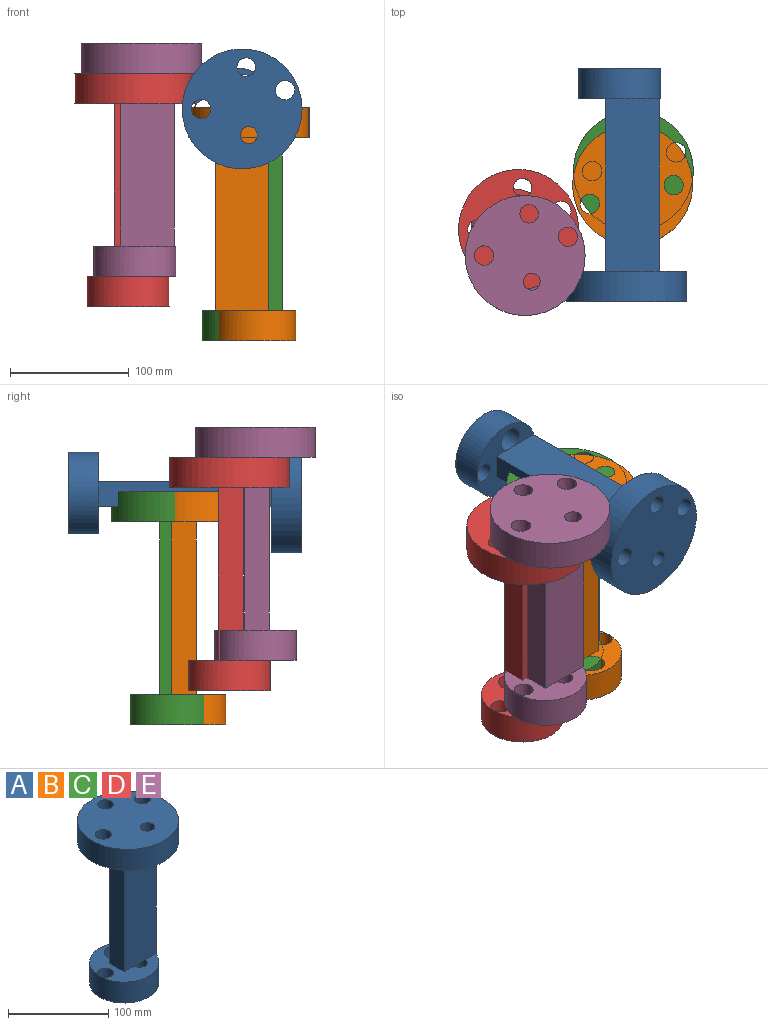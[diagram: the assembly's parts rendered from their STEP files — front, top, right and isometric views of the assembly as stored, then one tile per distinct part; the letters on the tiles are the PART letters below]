
ASSEMBLY  parts=5 mates=4
PART A: 21 faces, bbox 100.7x100.7x195.8 mm
  f0: plane 68.85x67.57mm, normal (0,0,1), area 2124.9mm2, adj f1,f2,f3,f4,f9,f11,f12
  f1: cylinder r=7.6mm len=25.4mm, axis (0,0,-1), area 1212.9mm2, adj f0,f6,f13
  f2: cylinder r=10.67mm len=25.4mm, axis (0,0,-1), area 1702.6mm2, adj f0,f6,f7
  f3: cylinder r=8.03mm len=25.4mm, axis (0,0,-1), area 1281.9mm2, adj f0,f6
  f4: cylinder r=34.42mm len=68.85mm, axis (0,0,-1), area 5493.9mm2, adj f0,f5,f6,f8
  f5: plane 18.6x1.28mm, normal (0,0,1), area 15.9mm2, adj f4,f10
  f6: plane 68.85x68.85mm, normal (0,0,-1), area 2981.3mm2, adj f1,f2,f3,f4
  f7: plane 10.27x1.32mm, normal (0,0,-1), area 9.1mm2, adj f2,f11
  f8: plane 2.37x0.76mm, normal (0,0,-1), area 0.9mm2, adj f4,f9,f10
  f9: plane 145.03x44.82mm, normal (0,-1,0), area 6501mm2, adj f0,f8,f10,f12,f13,f14
  f10: plane 145.03x20.97mm, normal (1,0,0), area 3041.6mm2, adj f5,f8,f9,f11,f14
  f11: plane 145.03x44.82mm, normal (0,1,0), area 6501mm2, adj f0,f7,f10,f12,f14
  f12: plane 145.03x20.97mm, normal (-1,0,0), area 3041.6mm2, adj f0,f9,f11,f14
  f13: plane 15.2x7.53mm, normal (0,0,-1), area 89.6mm2, adj f1,f9
  f14: plane 100.73x100.73mm, normal (0,0,-1), area 6263.4mm2, adj f9,f10,f11,f12,f15,f16,f17,f18
  f15: cylinder r=8.14mm len=25.4mm, axis (0,0,-1), area 1299.2mm2, adj f14,f20
  f16: cylinder r=7.12mm len=25.4mm, axis (0,0,-1), area 1136.1mm2, adj f14,f20
  f17: cylinder r=8.16mm len=25.4mm, axis (0,0,-1), area 1301.7mm2, adj f14,f20
  f18: cylinder r=7.78mm len=25.4mm, axis (0,0,-1), area 1240.9mm2, adj f14,f20
  f19: cylinder r=50.37mm len=100.73mm, axis (0,0,-1), area 8038.2mm2, adj f14,f20
  f20: plane 100.73x100.73mm, normal (0,0,1), area 7203.4mm2, adj f15,f16,f17,f18,f19
PART B: same geometry as A
PART C: same geometry as A
PART D: same geometry as A
PART E: same geometry as A
PLACE A rot(axis=(1,0,0),90deg) t=(10.47,92.71,119.97)mm
PLACE B rot(axis=(0,0,1),180deg) t=(-91.44,-5.21,-74.83)mm
PLACE C t=(16.52,6.54,-74.83)mm
PLACE D t=(-79.97,-42.58,-46.06)mm fixed
PLACE E t=(-74.42,-64.52,-20.66)mm
MATE fastened A.f9 <-> B.f19  axis (0,0,-1) through (-37.77,-5.21,108.3)mm
MATE fastened B.f1 <-> C.f4  axis (0,0,-1) through (-42.44,6.54,-74.83)mm
MATE fastened D.f16 <-> E.f19  axis (0,0,1) through (-128.09,-64.52,149.77)mm
MATE fastened E.f19 <-> E.f20  axis (0,0,-1) through (-128.09,-64.52,162.47)mm
